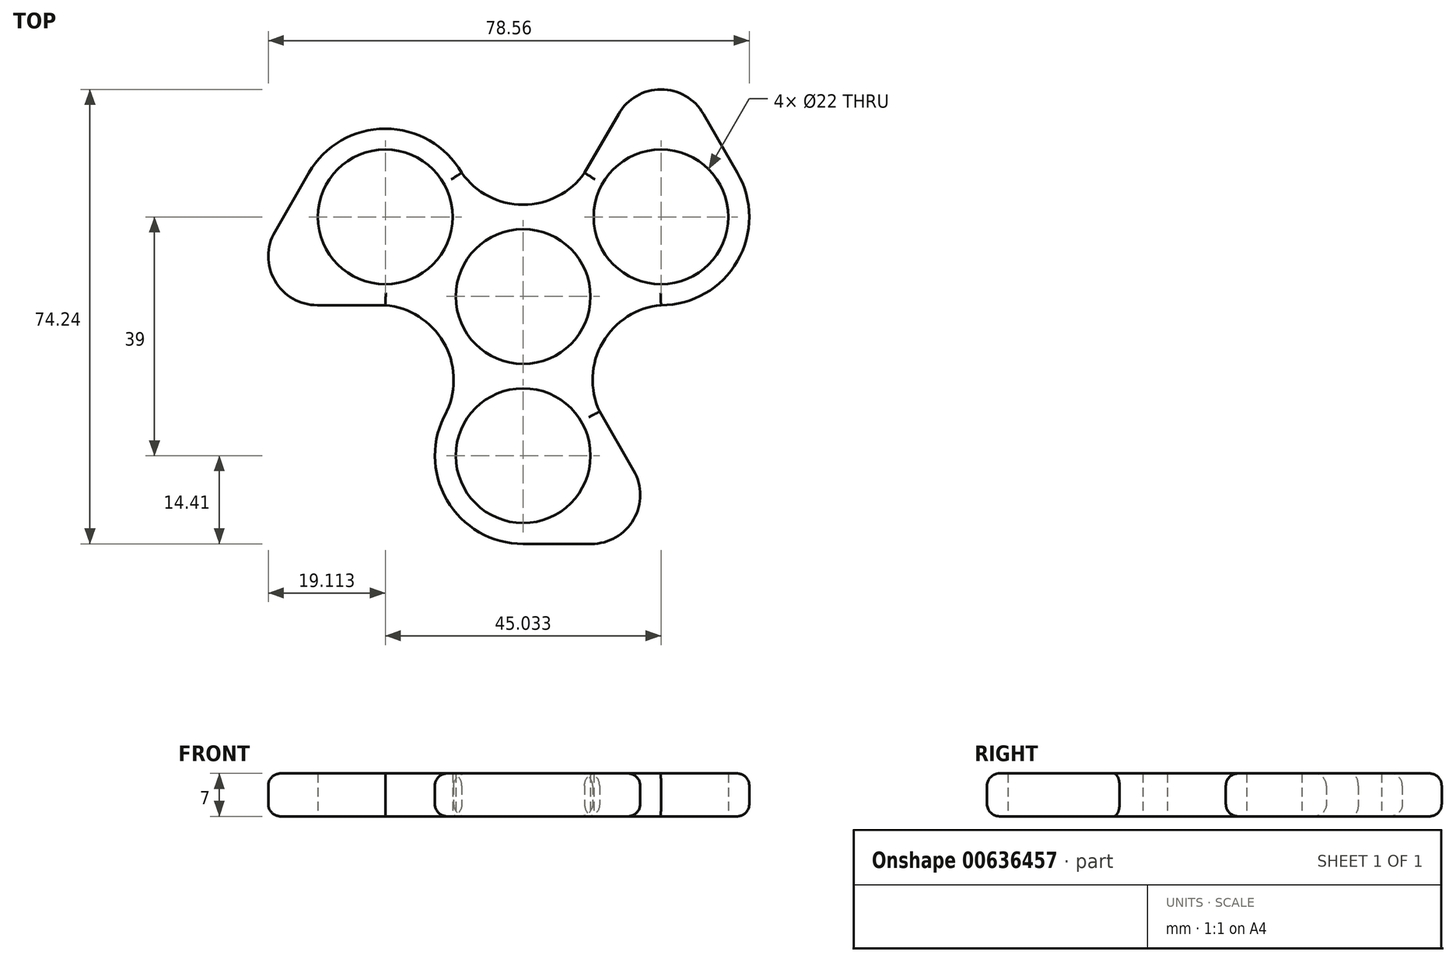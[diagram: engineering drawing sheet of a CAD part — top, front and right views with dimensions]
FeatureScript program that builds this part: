
annotation { "Feature Type Name" : "Feature", "Feature Type Description" : "" }
export const myFeature = defineFeature(function(context is Context, id is Id, definition is map)
    precondition{}
    {
        {
            var Q0;
            Q0=qCreatedBy(makeId("Top.planeOp"),FACE);
            var sketch = newSketch(context, id + "F0", { "sketchPlane" : qUnion([Q0])});
            skPoint(sketch, "E0.0.midPoint", {"position": v(0, 20.2) * mm});
            skCircle(sketch, "E1", {"center": v(0, 0) * mm, "radius": 11 * mm});
            skCircle(sketch, "E2", {"center": v(0, -26) * mm, "radius": 11 * mm});
            skCircle(sketch, "E3", {"center": v(-22.52, 13) * mm, "radius": 11 * mm});
            skCircle(sketch, "E4", {"center": v(22.52, 13) * mm, "radius": 11 * mm});
            skArc(sketch, "E5", {"start": v(22.52, -1.41) * mm, "mid": v(35, 5.8) * mm, "end": v(35, 20.2) * mm});
            skArc(sketch, "E6", {"start": v(-10.03, 20.2) * mm, "mid": v(-22.52, 27.41) * mm, "end": v(-35, 20.2) * mm});
            skArc(sketch, "E7", {"start": v(-12.48, -18.8) * mm, "mid": v(-12.48, -33.2) * mm, "end": v(0, -40.41) * mm});
            skArc(sketch, "E8", {"start": v(22.52, -1.41) * mm, "mid": v(13, -7.5) * mm, "end": v(12.48, -18.8) * mm});
            skArc(sketch, "E9", {"start": v(-12.48, -18.8) * mm, "mid": v(-13, -7.5) * mm, "end": v(-22.52, -1.41) * mm});
            skArc(sketch, "E10", {"start": v(-10.03, 20.2) * mm, "mid": v(0, 15) * mm, "end": v(10.03, 20.2) * mm});
            skArc(sketch, "E11.cCircle", {"start": v(-12.48, -18.8) * mm, "mid": v(-12.48, -33.2) * mm, "end": v(0, -40.41) * mm, "construction": true});
            skLineSegment(sketch, "E11.1", {"start": v(11.11, -40.41) * mm, "end": v(0, -40.41) * mm});
            skPoint(sketch, "E11.0.midPoint", {"position": v(12.48, -18.8) * mm});
            skLineSegment(sketch, "E12.trimOffspring", {"start": v(12.48, -18.8) * mm, "end": v(18.04, -28.41) * mm});
            skPoint(sketch, "E13.trimOffspring.end.orphan", {"position": v(0, 2.83) * mm});
            skPoint(sketch, "E14.visualSharp", {"position": v(24.97, -40.41) * mm});
            skArc(sketch, "E15.cCircle", {"start": v(20.17, -1.22) * mm, "mid": v(34.37, 4.8) * mm, "end": v(35, 20.2) * mm, "construction": true});
            skLineSegment(sketch, "E15.0", {"start": v(22.52, -1.41) * mm, "end": v(20.16, -1.41) * mm, "construction": true});
            skLineSegment(sketch, "E15.2", {"start": v(29.44, 29.83) * mm, "end": v(35, 20.2) * mm, "construction": true});
            skPoint(sketch, "E15.0.midPoint", {"position": v(22.52, -1.41) * mm});
            skLineSegment(sketch, "E16.trimOffspring", {"start": v(8.85, 18.16) * mm, "end": v(15.59, 29.83) * mm, "construction": true});
            skPoint(sketch, "E15.1.start.orphan", {"position": v(-2.45, -1.41) * mm});
            skPoint(sketch, "E17.orphan", {"position": v(47.48, -1.41) * mm});
            skPoint(sketch, "E18.visualSharp", {"position": v(22.52, 41.83) * mm});
            skArc(sketch, "E18.filletArc", {"start": v(29.44, 29.83) * mm, "mid": v(22.52, 33.83) * mm, "end": v(15.59, 29.83) * mm, "construction": true});
            skLineSegment(sketch, "E19", {"start": v(35, 20.2) * mm, "end": v(29.44, 29.83) * mm});
            skLineSegment(sketch, "E20", {"start": v(15.59, 29.83) * mm, "end": v(10.03, 20.2) * mm});
            skLineSegment(sketch, "E21", {"start": v(15.59, 29.83) * mm, "end": v(15.59, 29.83) * mm});
            skLineSegment(sketch, "E22", {"start": v(29.44, 29.83) * mm, "end": v(29.44, 29.83) * mm});
            skArc(sketch, "E23.filletArc", {"start": v(29.44, 29.83) * mm, "mid": v(22.52, 33.83) * mm, "end": v(15.59, 29.83) * mm});
            skLineSegment(sketch, "E24.1", {"start": v(-40.56, 10.59) * mm, "end": v(-35, 20.2) * mm, "construction": true});
            skPoint(sketch, "E24.0.midPoint", {"position": v(-22.52, -1.41) * mm});
            skPoint(sketch, "E25.visualSharp", {"position": v(-47.48, -1.41) * mm});
            skArc(sketch, "E25.filletArc", {"start": v(-40.56, 10.59) * mm, "mid": v(-40.56, 2.59) * mm, "end": v(-33.63, -1.41) * mm, "construction": true});
            skLineSegment(sketch, "E26", {"start": v(-35, 20.2) * mm, "end": v(-40.56, 10.59) * mm});
            skLineSegment(sketch, "E27", {"start": v(-22.52, -1.41) * mm, "end": v(-33.63, -1.41) * mm});
            skLineSegment(sketch, "E28", {"start": v(-33.63, -1.41) * mm, "end": v(-33.63, -1.41) * mm});
            skLineSegment(sketch, "E29", {"start": v(-40.56, 10.59) * mm, "end": v(-40.56, 10.59) * mm});
            skArc(sketch, "E30.filletArc", {"start": v(-40.56, 10.59) * mm, "mid": v(-40.56, 2.59) * mm, "end": v(-33.63, -1.41) * mm});
            skLineSegment(sketch, "E31.trimOffspring", {"start": v(-22.52, -1.41) * mm, "end": v(-33.63, -1.41) * mm, "construction": true});
            skPoint(sketch, "E32.orphan", {"position": v(2.45, -1.41) * mm});
            skArc(sketch, "E33", {"start": v(11.11, -40.41) * mm, "mid": v(18.04, -36.41) * mm, "end": v(18.04, -28.41) * mm});
            skSolve(sketch);
        }
        {
            var Q0;
            Q0=makeQuery(id+"F0.imprint","IMPRINT",FACE,{"disambiguationData":[TD([[makeQuery(id+"F0.imprint","IMPRINT",EDGE,{"derivedFrom":sQuery(id+"F0.wireOp",EDGE,"E1")}),-1.0]])]});
            extrude(context, id + "F1", {"entities" : qUnion([Q0]), "depth" : 7 * mm, "offsetDistance" : 25 * mm});
        }
        {
            var Q0;
            Q0=makeQuery(id+"F1.opExtrude","CAP_EDGE",EDGE,{"disambiguationData":[OSD([sQuery(id+"F0.wireOp",EDGE,"E8")])],"isStart":false});
            var Q1;
            Q1=makeQuery(id+"F1.opExtrude","CAP_EDGE",EDGE,{"disambiguationData":[OSD([sQuery(id+"F0.wireOp",EDGE,"E8")])],"isStart":true});
            var Q2;
            Q2=makeQuery(id+"F1.opExtrude","CAP_EDGE",EDGE,{"disambiguationData":[OSD([sQuery(id+"F0.wireOp",EDGE,"E9")])],"isStart":false});
            var Q3;
            Q3=makeQuery(id+"F1.opExtrude","CAP_EDGE",EDGE,{"disambiguationData":[OSD([sQuery(id+"F0.wireOp",EDGE,"E9")])],"isStart":true});
            var Q4;
            Q4=makeQuery(id+"F1.opExtrude","CAP_EDGE",EDGE,{"disambiguationData":[OSD([sQuery(id+"F0.wireOp",EDGE,"E10")])],"isStart":true});
            var Q5;
            Q5=makeQuery(id+"F1.opExtrude","CAP_EDGE",EDGE,{"disambiguationData":[OSD([sQuery(id+"F0.wireOp",EDGE,"E10")])],"isStart":false});
            var Q6;
            Q6=makeQuery(id+"F1.opExtrude","CAP_EDGE",EDGE,{"disambiguationData":[OSD([sQuery(id+"F0.wireOp",EDGE,"E23.filletArc")])],"isStart":true});
            var Q7;
            Q7=makeQuery(id+"F1.opExtrude","CAP_EDGE",EDGE,{"disambiguationData":[OSD([sQuery(id+"F0.wireOp",EDGE,"E23.filletArc")])],"isStart":false});
            var Q8;
            Q8=makeQuery(id+"F1.opExtrude","CAP_EDGE",EDGE,{"disambiguationData":[OSD([sQuery(id+"F0.wireOp",EDGE,"E6")])],"isStart":false});
            var Q9;
            Q9=makeQuery(id+"F1.opExtrude","CAP_EDGE",EDGE,{"disambiguationData":[OSD([sQuery(id+"F0.wireOp",EDGE,"E6")])],"isStart":true});
            var Q10;
            Q10=makeQuery(id+"F1.opExtrude","SWEPT_FACE",FACE,{"disambiguationData":[OSD([sQuery(id+"F0.wireOp",EDGE,"E7")])]});
            fillet(context, id + "F2", {"entities" : qUnion([Q0, Q1, Q2, Q3, Q4, Q5, Q6, Q7, Q8, Q9, Q10]), "radius" : 2 * mm, "tangentPropagation" : true, "allowEdgeOverflow" : false});
        }
    });
